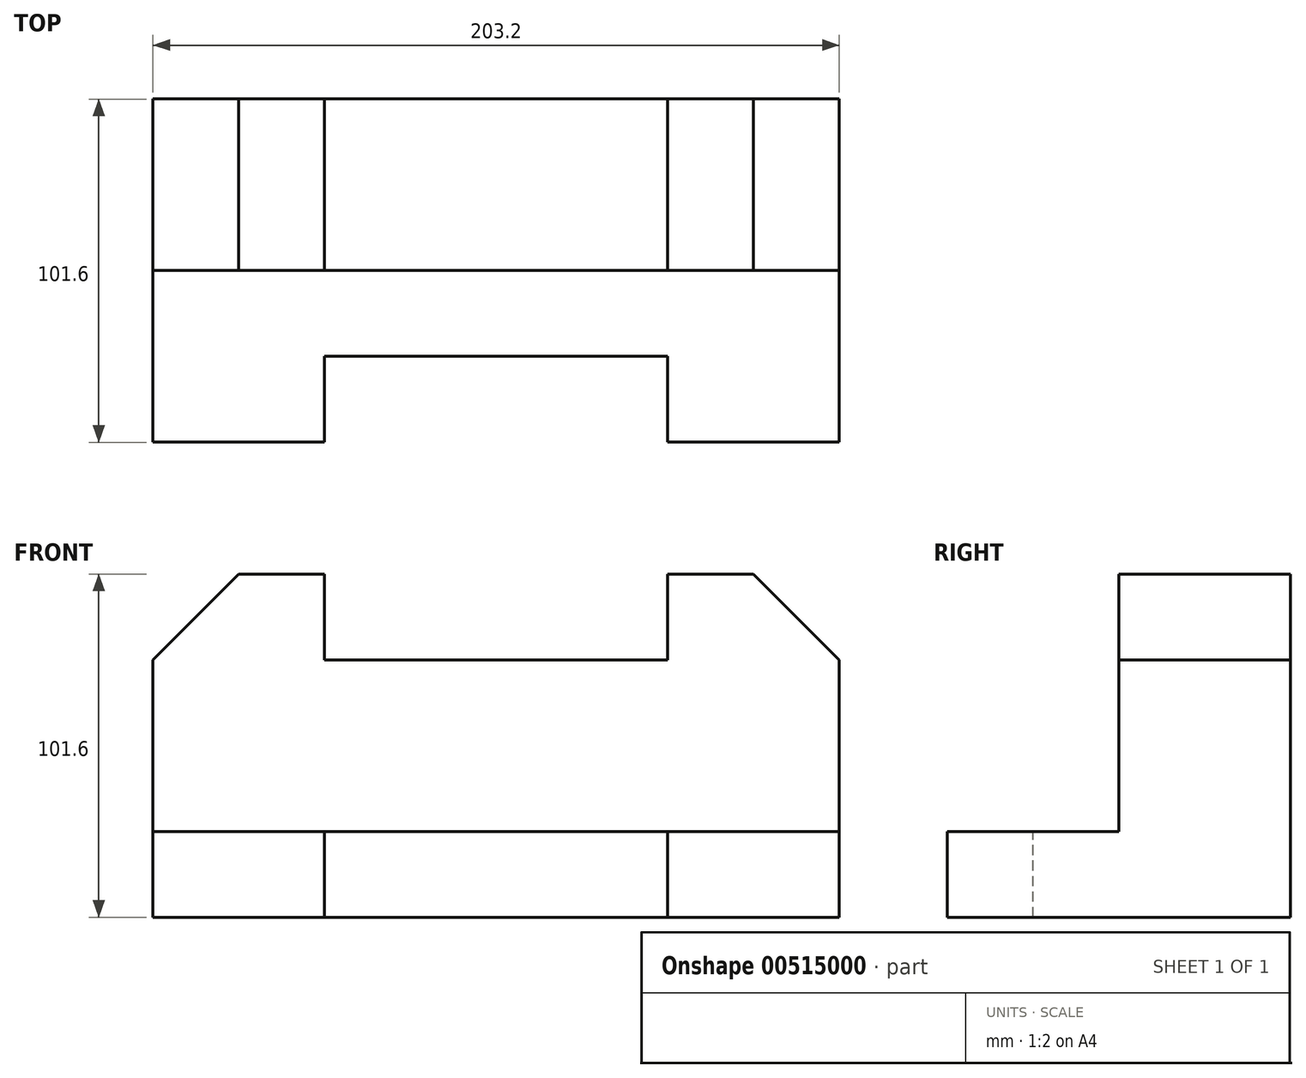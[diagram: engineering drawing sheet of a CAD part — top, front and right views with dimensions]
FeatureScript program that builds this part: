
annotation { "Feature Type Name" : "Feature", "Feature Type Description" : "" }
export const myFeature = defineFeature(function(context is Context, id is Id, definition is map)
    precondition{}
    {
        {
            var Q0;
            Q0=qCreatedBy(makeId("Top.planeOp"),FACE);
            var sketch = newSketch(context, id + "F0", { "sketchPlane" : qUnion([Q0])});
            skLineSegment(sketch, "E0.bottom", {"start": v(-95.72, 32.2) * mm, "end": v(-44.92, 32.2) * mm});
            skLineSegment(sketch, "E0.top", {"start": v(-95.72, -69.4) * mm, "end": v(-44.92, -69.4) * mm});
            skLineSegment(sketch, "E0.left", {"start": v(-95.72, 32.2) * mm, "end": v(-95.72, -69.4) * mm});
            skLineSegment(sketch, "E0.right", {"start": v(107.48, 32.2) * mm, "end": v(107.48, -69.4) * mm});
            skLineSegment(sketch, "E1", {"start": v(-44.92, -69.4) * mm, "end": v(56.68, -69.4) * mm});
            skLineSegment(sketch, "E2", {"start": v(56.68, -69.4) * mm, "end": v(107.48, -69.4) * mm});
            skLineSegment(sketch, "E3", {"start": v(-44.92, 32.2) * mm, "end": v(56.68, 32.2) * mm});
            skLineSegment(sketch, "E4", {"start": v(56.68, 32.2) * mm, "end": v(107.48, 32.2) * mm});
            skSolve(sketch);
        }
        {
            var Q0;
            Q0 = qSketchRegion(id + "F0", true);
            extrude(context, id + "F1", {"entities" : qUnion([Q0]), "depth" : 101.6 * mm, "offsetDistance" : 25.4 * mm});
        }
        {
            var Q0;
            Q0=makeQuery(id+"F1.opExtrude","CAP_FACE",FACE,{"disambiguationData":[OSD([sQuery(id+"F0.wireOp",EDGE,"E0.bottom"),sQuery(id+"F0.wireOp",EDGE,"E0.top"),sQuery(id+"F0.wireOp",EDGE,"E0.left"),sQuery(id+"F0.wireOp",EDGE,"E0.right")])],"isStart":false});
            var sketch = newSketch(context, id + "F2", { "sketchPlane" : qUnion([Q0])});
            skLineSegment(sketch, "E5.bottom", {"start": v(-95.72, -69.4) * mm, "end": v(107.48, -69.4) * mm});
            skLineSegment(sketch, "E5.top", {"start": v(-95.72, -18.6) * mm, "end": v(107.48, -18.6) * mm});
            skLineSegment(sketch, "E5.left", {"start": v(-95.72, -69.4) * mm, "end": v(-95.72, -18.6) * mm});
            skLineSegment(sketch, "E5.right", {"start": v(107.48, -69.4) * mm, "end": v(107.48, -18.6) * mm});
            skSolve(sketch);
        }
        {
            var Q0;
            Q0 = qSketchRegion(id + "F2", true);
            extrude(context, id + "F3", {"entities" : qUnion([Q0]), "operationType" : NewBodyOperationType.REMOVE, "oppositeDirection" : true, "depth" : 76.2 * mm, "offsetDistance" : 25.4 * mm});
        }
        {
            var Q0;
            Q0=makeQuery(id+"F3.boolean.opBoolean","COPY",FACE,{"derivedFrom":makeQuery(id+"F3.opExtrude","CAP_FACE",FACE,{"disambiguationData":[OSD([sQuery(id+"F2.wireOp",EDGE,"E5.bottom"),sQuery(id+"F2.wireOp",EDGE,"E5.top"),sQuery(id+"F2.wireOp",EDGE,"E5.left"),sQuery(id+"F2.wireOp",EDGE,"E5.right")])],"isStart":false})});
            var sketch = newSketch(context, id + "F4", { "sketchPlane" : qUnion([Q0])});
            skLineSegment(sketch, "E6.bottom", {"start": v(-44.92, -69.4) * mm, "end": v(56.68, -69.4) * mm});
            skLineSegment(sketch, "E6.top", {"start": v(-44.92, -44) * mm, "end": v(56.68, -44) * mm});
            skLineSegment(sketch, "E6.left", {"start": v(-44.92, -69.4) * mm, "end": v(-44.92, -44) * mm});
            skLineSegment(sketch, "E6.right", {"start": v(56.68, -69.4) * mm, "end": v(56.68, -44) * mm});
            skSolve(sketch);
        }
        {
            var Q0;
            Q0 = qSketchRegion(id + "F4", true);
            extrude(context, id + "F5", {"entities" : qUnion([Q0]), "operationType" : NewBodyOperationType.REMOVE, "oppositeDirection" : true, "depth" : 25.4 * mm, "offsetDistance" : 25.4 * mm});
        }
        {
            var Q0;
            Q0=makeQuery(id+"F1.opExtrude","CAP_FACE",FACE,{"disambiguationData":[OSD([sQuery(id+"F0.wireOp",EDGE,"E0.bottom"),sQuery(id+"F0.wireOp",EDGE,"E0.top"),sQuery(id+"F0.wireOp",EDGE,"E0.left"),sQuery(id+"F0.wireOp",EDGE,"E0.right"),sQuery(id+"F0.wireOp",EDGE,"E1"),sQuery(id+"F0.wireOp",EDGE,"E2"),sQuery(id+"F0.wireOp",EDGE,"E3"),sQuery(id+"F0.wireOp",EDGE,"E4")])],"isStart":false});
            var sketch = newSketch(context, id + "F6", { "sketchPlane" : qUnion([Q0])});
            skLineSegment(sketch, "E7.bottom", {"start": v(-44.92, 32.2) * mm, "end": v(56.68, 32.2) * mm});
            skLineSegment(sketch, "E7.top", {"start": v(-44.92, -18.6) * mm, "end": v(56.68, -18.6) * mm});
            skLineSegment(sketch, "E7.left", {"start": v(-44.92, 32.2) * mm, "end": v(-44.92, -18.6) * mm});
            skLineSegment(sketch, "E7.right", {"start": v(56.68, 32.2) * mm, "end": v(56.68, -18.6) * mm});
            skSolve(sketch);
        }
        {
            var Q0;
            Q0 = qSketchRegion(id + "F6", true);
            extrude(context, id + "F7", {"entities" : qUnion([Q0]), "operationType" : NewBodyOperationType.REMOVE, "oppositeDirection" : true, "depth" : 25.4 * mm, "offsetDistance" : 25.4 * mm});
        }
        {
            var Q0;
            Q0=makeQuery(id+"F1.opExtrude","CAP_EDGE",EDGE,{"disambiguationData":[OSD([sQuery(id+"F0.wireOp",EDGE,"E0.right")])],"isStart":false});
            chamfer(context, id + "F8", {"entities" : qUnion([Q0]), "width" : 25.4 * mm, "tangentPropagation" : true});
        }
        {
            var Q0;
            Q0=makeQuery(id+"F1.opExtrude","CAP_EDGE",EDGE,{"disambiguationData":[OSD([sQuery(id+"F0.wireOp",EDGE,"E0.left")])],"isStart":false});
            chamfer(context, id + "F9", {"entities" : qUnion([Q0]), "width" : 25.4 * mm, "tangentPropagation" : true});
        }
    });
